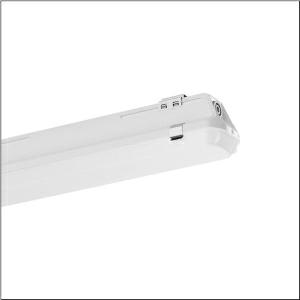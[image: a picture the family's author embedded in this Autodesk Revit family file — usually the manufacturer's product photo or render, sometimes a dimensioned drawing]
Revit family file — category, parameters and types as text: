
# Revit family: monsun_r__21_emergency_51fb10dp437b3h_9196
name_source: partatom
category: Lighting Fixtures
units: mm (PartAtom-declared; Revit-internal decimal feet)

## family parameters
Cut with Voids When Loaded = No
Host = Face
Light Source = No
Part Type = Normal
Room Calculation Point = No
Round Connector Dimension = Use Diameter
Shared = No

## types (1)
- --- (1 x LED, 3860 lm, 27.5 W, 4000K)
    Apparent Load = 28 VA
    CIE Flux Codes = 47 77 93 94 100
    Color Rendering = 80
    Color Temperature = 4000K
    Default Elevation = 1800 mm
    Description = Monsun® 21 emergency, damp-proof luminaire, chain hanger, primary optical cover: enclosure, of PMMA, light emission: direct distribution, primary light characteristic: symmetric, installation type: vertical mounting, horizontal mounting, surface-mounted, suspended mounting, LED, rated luminous flux: 3.860lm, luminous efficacy: 140lm/W, light colour: 840, colour temperature: 4000K, control gear: ECG DALI, with terminal, 5+3-pole, max. 2.5mm², mains connection: 220..240V, AC, 50/60Hz, rated input power: 28W, control gear: single battery element, battery: NiCd, 4,5Ah, mains connection: 230V, housing, of glass-fibre reinforced polyester, uncoated, bright grey, incl. chain hanger, length: 1.590mm, width: 90mm, height: 88mm, clip for enclosure, of stainless steel (V2A), ceiling mounting element, of stainless steel (V2A), chain hanger, of stainless steel (V2A), protection rating (complete): IP66, insulation class (complete): insulation class I (protective earthing), certification: CE, UKCA, protection symbol: D, impact resistance: IK04, permissible operating ambient temperature: +5..+25°C, standard: EN 60598-2-1, EN 50419, EN 60598-2-22, corresponds to IFS (International Featured Standards) requirements for safety and quality in the food industry, for indoor or canopied outdoor use, no direct snow, no direct sun, no direct rain, contact your sales advisor before using the luminaires in applications with unclear chemical exposure, large temperature fluctuations or condensation-forming humidity, LABS conformity tested according to VDMA 24364:2018-05, packaging unit: 1 piece
    Height = 89 mm
    Lamp = 1 x LED
    Lamp Light Flux = 3860 lm
    Lamp Power = 27.5 W
    Lamp count = 1
    Length = 1590 mm
    Luminous efficacy = 140 lm/W
    Manufacturer = Siteco
    ModVariant = No
    Model = 51FB10DP437B3H
    Mounting Place = Ceiling
    Mounting Type = Surface mounted
    Number of Poles = 1
    OnlyDefault = Yes
    Power Factor = 1
    Product Name = Monsun® 21 emergency
    Product group = damp-proof luminaire
    ProductGroupID = 300
    Protection Class = Protection class I
    Protection Degree = IP 66
    RLX_Detail_Level = 1
    RLX_Emergency_Light_Flux = 0 lm
    RLX_Emergency_Type = 0
    RLX_Emergency_Type_DB = No
    RlxData = <blob elided: 92877 chars, md5=04d302e8>
    Socket = socket
    Standby Power = 0 W
    System Light Flux = 3860 lm
    System Power = 28 W
    Type Comments = factory setting: luminous flux: 100 % | dim-lin: 254 | 162 mA
    Type Image = l_1006717.jpg
    URL = http://relux.com
    VarID = @adj_134173
    Voltage = 0 V
    Weight = 0.00 kg
    Width = 90 mm

## geometry (parser evidence)
native form markers: Blend x4, Sweep x13
no freeform markers — native parametric forms only
